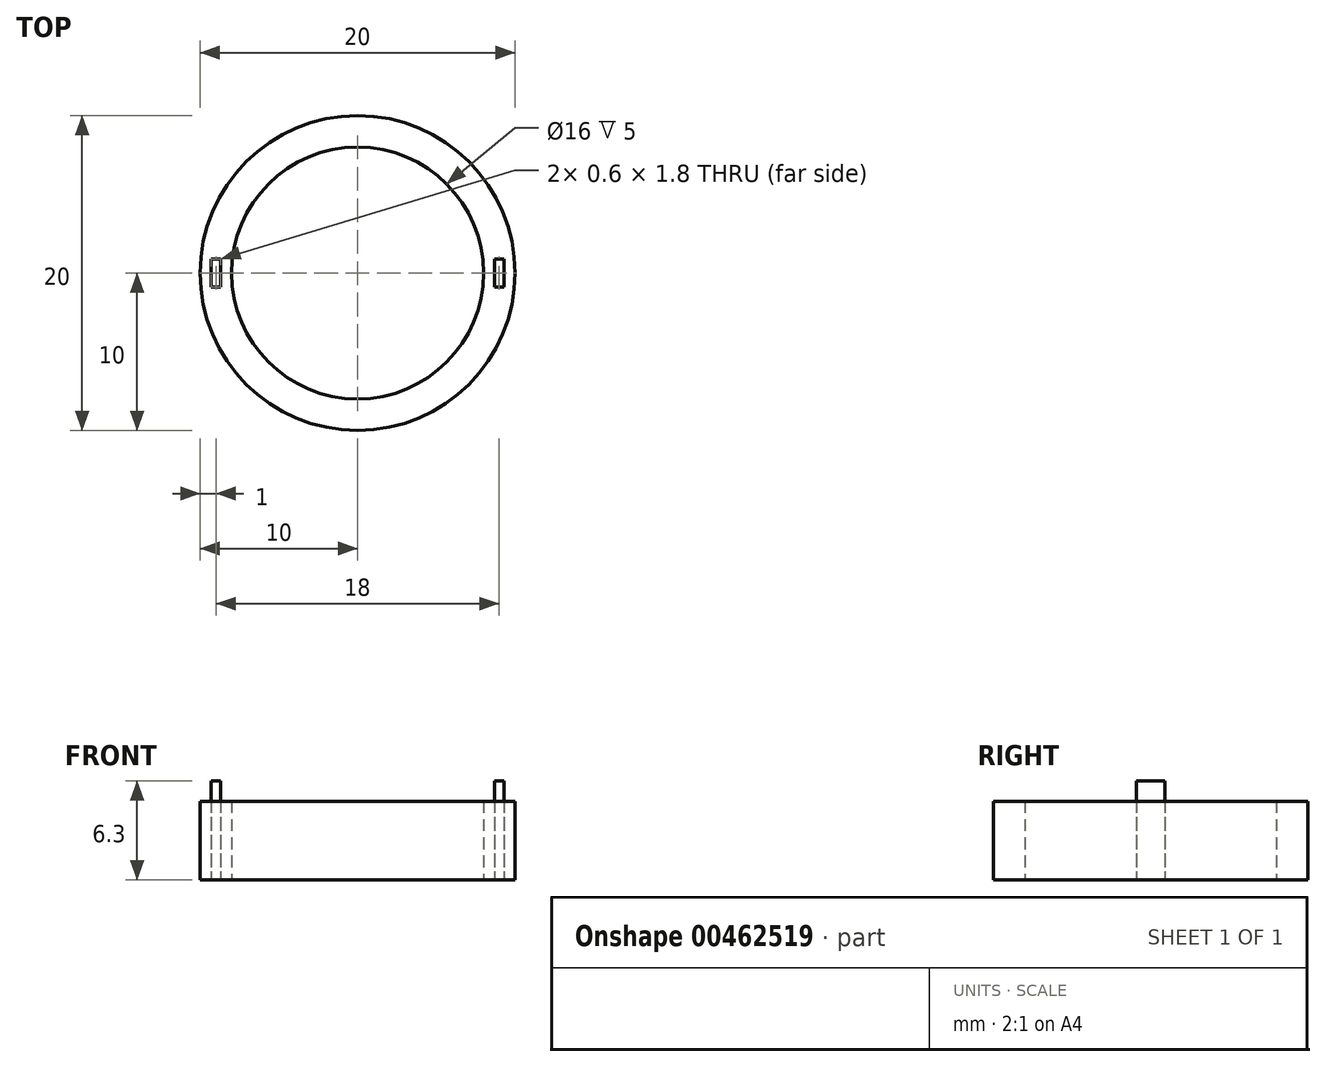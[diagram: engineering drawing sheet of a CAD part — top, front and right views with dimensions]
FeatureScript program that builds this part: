
annotation { "Feature Type Name" : "Feature", "Feature Type Description" : "" }
export const myFeature = defineFeature(function(context is Context, id is Id, definition is map)
    precondition{}
    {
        {
            var Q0;
            Q0=qCreatedBy(makeId("Top.planeOp"),FACE);
            var sketch = newSketch(context, id + "F0", { "sketchPlane" : qUnion([Q0])});
            skCircle(sketch, "E0", {"center": v(0, 0) * mm, "radius": 10 * mm});
            skLineSegment(sketch, "E1.bottom", {"start": v(-9.3, 0.9) * mm, "end": v(-8.7, 0.9) * mm});
            skLineSegment(sketch, "E1.top", {"start": v(-9.3, -0.9) * mm, "end": v(-8.7, -0.9) * mm});
            skLineSegment(sketch, "E1.left", {"start": v(-9.3, 0.9) * mm, "end": v(-9.3, -0.9) * mm});
            skLineSegment(sketch, "E1.right", {"start": v(-8.7, 0.9) * mm, "end": v(-8.7, -0.9) * mm});
            skLineSegment(sketch, "E2.bottom", {"start": v(8.7, 0.9) * mm, "end": v(9.3, 0.9) * mm});
            skLineSegment(sketch, "E2.top", {"start": v(8.7, -0.9) * mm, "end": v(9.3, -0.9) * mm});
            skLineSegment(sketch, "E2.left", {"start": v(8.7, 0.9) * mm, "end": v(8.7, -0.9) * mm});
            skLineSegment(sketch, "E2.right", {"start": v(9.3, 0.9) * mm, "end": v(9.3, -0.9) * mm});
            skCircle(sketch, "E3", {"center": v(0, 0) * mm, "radius": 8 * mm});
            skSolve(sketch);
        }
        {
            var Q0;
            Q0=makeQuery(id+"F0.imprint","IMPRINT",FACE,{"disambiguationData":[TD([[makeQuery(id+"F0.imprint","IMPRINT",EDGE,{"derivedFrom":sQuery(id+"F0.wireOp",EDGE,"E1.bottom")}),-1.0]])]});
            var Q1;
            Q1=makeQuery(id+"F0.imprint","IMPRINT",FACE,{"disambiguationData":[TD([[makeQuery(id+"F0.imprint","IMPRINT",EDGE,{"derivedFrom":sQuery(id+"F0.wireOp",EDGE,"E2.bottom")}),-1.0]])]});
            extrude(context, id + "F1", {"entities" : qUnion([Q0, Q1]), "depth" : 6.3 * mm});
        }
        {
            var Q0;
            Q0=qSketchRegion(id+"F0",true);
            extrude(context, id + "F2", {"entities" : qUnion([Q0]), "depth" : 5 * mm});
        }
    });
